# Revit family: PRD_FrankeWS_SnkMnlWtrSpplSts_SIRIUSSiphonCover_SIRX514
name_source: partatom
category: Furniture
revit_build: Autodesk Revit 2018 (Build: 20190510_1515(x64)
units: mm (PartAtom-declared; Revit-internal decimal feet)

## family parameters
Cut with Voids When Loaded = No
Host = Face
OmniClass Number = 23.45.05.14.99
OmniClass Title = Other Sanitary Washing Plumbing Fixtures
Room Calculation Point = No
Shared = No

## types (1)
- SIRX514
    AssetType = Fixed
    BIMObjectName = PRD_AR_SinkManualWaterSupplySets_SIRIUSSiphonCover_SIRX514
    Category = Pr_40_20_87_82, Sink manual water supply sets
    Default Elevation = 1000 mm  [stored 3.28084 ft]
    Description = Siphon cover for disposal sink made of MIRANIT for wall mounting, made of nickel-chromium steel, fastening material included.
    DurationUnit = year
    Features = nickel-chromium steel
    Finish = Nickel-chromed
    GrossWeight = 1.76 kg
    IfcExportAs = IfcSanitaryTerminalType
    IfcExportType = USERDEFINED
    IntegralAccessories = fastening material incl.
    MainColor = stainless steel
    MainMaterial = PRD_AR_Steel_NickelChromed
    Manufacturer = KWC Group AG
    ManufacturerName = KWC Group AG
    ManufacturerURL = www.kwc.com
    Material = Steel
    Model = SIRX514
    ModelNumber = 2000101202
    ModelReference = SIRX514
    NBSDescription = Water supply fittings for sinks
    NBSReference = 45-35-70/345
    Name = SIRIUS Siphon cover SIRX514
    NetWeight = 1.67 kg
    NominalDepth = 341 mm
    NominalHeight = 287 mm  [stored 0.941601 ft]
    NominalLength = 0 mm  [stored 0 ft]
    NominalWidth = 145 mm  [stored 0.475722 ft]
    ProductCode = 207.0638.422
    ProductInformation = https://pim.kwc.com
    Quantity = 1
    QuantityUom = Piece
    Size = 145 x 287 x 341 mm (W x H x D)
    Status = New
    TailorMade = No
    URL = www.kwc.com
    Uniclass2015Code = Pr_40_20_87_82
    Uniclass2015Title = Sink manual water supply sets
    Uniclass2015Version = Products v1.17
    Version = 1
    WarrantyDurationUnit = year

note: [stored X ft] marks values corroborated as IEEE doubles in the binary element streams (Revit-internal decimal feet)

## geometry (parser evidence)
native form markers: Sweep x2
no freeform markers — native parametric forms only
